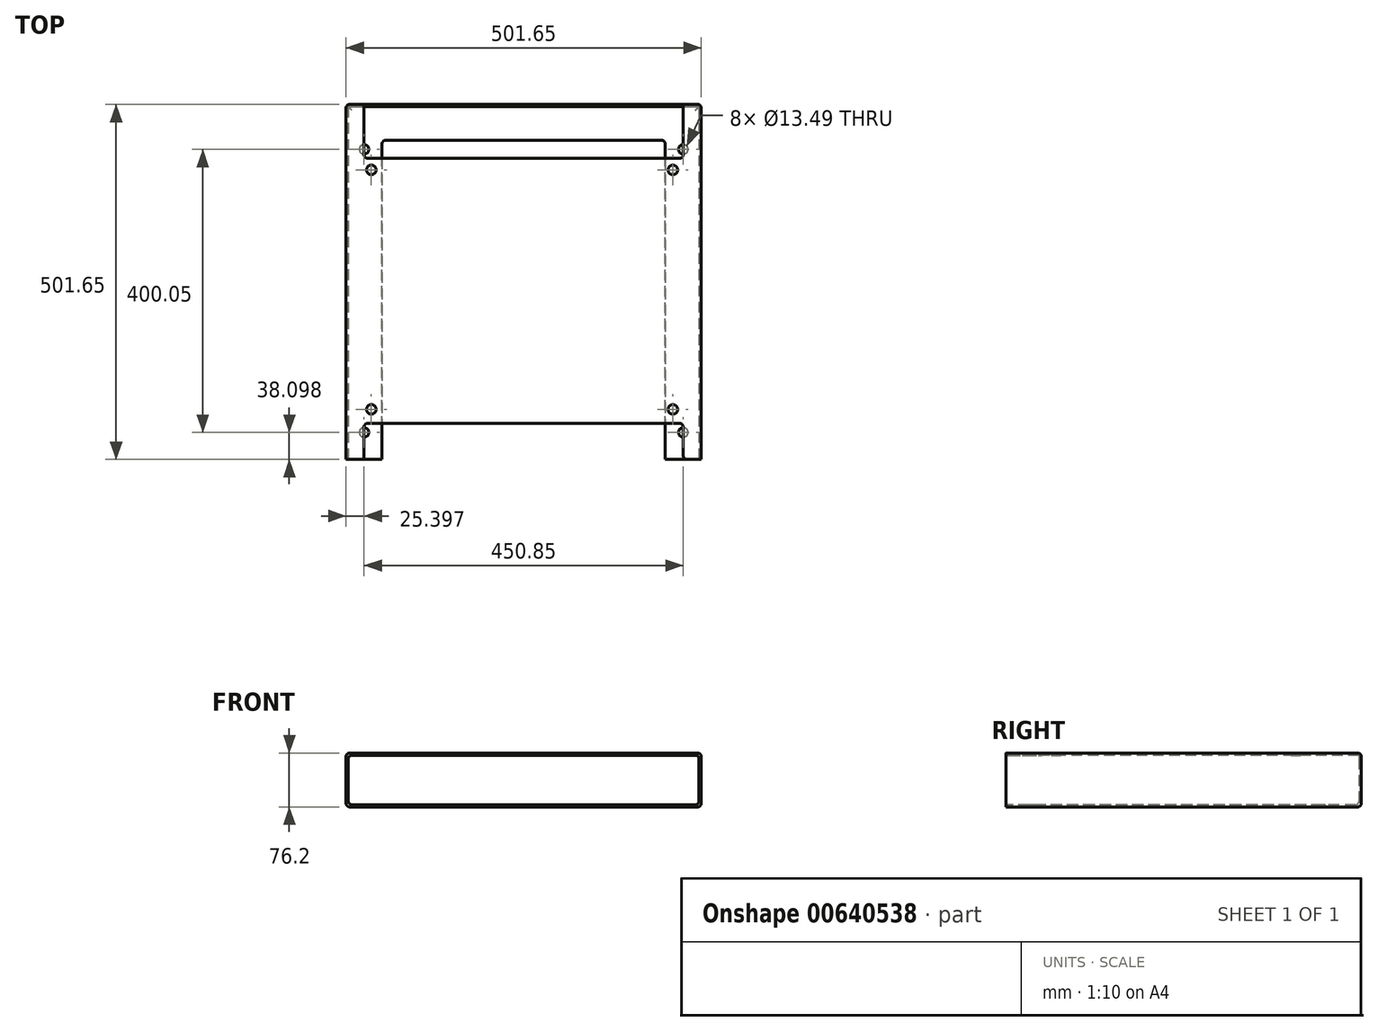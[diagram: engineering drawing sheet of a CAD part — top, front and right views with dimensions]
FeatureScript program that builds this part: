
annotation { "Feature Type Name" : "Feature", "Feature Type Description" : "" }
export const myFeature = defineFeature(function(context is Context, id is Id, definition is map)
    precondition{}
    {
        {
            var Q0;
            Q0=qCreatedBy(makeId("Top.planeOp"),FACE);
            var sketch = newSketch(context, id + "F0", { "sketchPlane" : qUnion([Q0])});
            skLineSegment(sketch, "E0.bottom", {"start": v(-248.23, 375.82) * mm, "end": v(253.42, 375.82) * mm});
            skLineSegment(sketch, "E0.top", {"start": v(-248.23, -125.83) * mm, "end": v(253.42, -125.83) * mm});
            skLineSegment(sketch, "E0.left", {"start": v(-248.23, 375.82) * mm, "end": v(-248.23, -125.83) * mm});
            skLineSegment(sketch, "E0.right", {"start": v(253.42, 375.82) * mm, "end": v(253.42, -125.83) * mm});
            skSolve(sketch);
        }
        {
            var Q0;
            Q0 = qSketchRegion(id + "F0", true);
            extrude(context, id + "F1", {"entities" : qUnion([Q0]), "depth" : 76.2 * mm, "offsetDistance" : 25.4 * mm});
        }
        {
            var Q0;
            Q0=makeQuery(id+"F1.opExtrude","SWEPT_FACE",FACE,{"disambiguationData":[OSD([sQuery(id+"F0.wireOp",EDGE,"E0.top")])]});
            shell(context, id + "F2", {"entities" : qUnion([Q0]), "thickness" : 3.17 * mm});
        }
        {
            var Q0;
            Q0=makeQuery(id+"F1.opExtrude","CAP_FACE",FACE,{"disambiguationData":[OSD([sQuery(id+"F0.wireOp",EDGE,"E0.bottom"),sQuery(id+"F0.wireOp",EDGE,"E0.top"),sQuery(id+"F0.wireOp",EDGE,"E0.left"),sQuery(id+"F0.wireOp",EDGE,"E0.right")])],"isStart":true});
            var sketch = newSketch(context, id + "F3", { "sketchPlane" : qUnion([Q0])});
            skLineSegment(sketch, "E1.bottom", {"start": v(-197.43, 125.83) * mm, "end": v(202.62, 125.83) * mm});
            skLineSegment(sketch, "E1.top", {"start": v(-197.43, -325.02) * mm, "end": v(202.62, -325.02) * mm});
            skLineSegment(sketch, "E1.left", {"start": v(-197.43, 125.83) * mm, "end": v(-197.43, -325.02) * mm});
            skLineSegment(sketch, "E1.right", {"start": v(202.62, 125.83) * mm, "end": v(202.62, -325.02) * mm});
            skSolve(sketch);
        }
        {
            var Q0;
            Q0 = qSketchRegion(id + "F3", true);
            extrude(context, id + "F4", {"entities" : qUnion([Q0]), "operationType" : NewBodyOperationType.REMOVE, "oppositeDirection" : true, "depth" : 25.4 * mm, "offsetDistance" : 25.4 * mm});
        }
        {
            var Q0;
            {var subQ0=sQuery(id+"F0.wireOp",EDGE,"E0.right");var subQ1=sQuery(id+"F0.wireOp",EDGE,"E0.left");var subQ2=sQuery(id+"F0.wireOp",EDGE,"E0.top");var subQ3=sQuery(id+"F0.wireOp",EDGE,"E0.bottom");Q0=makeQuery(id+"F2.opShell","OFFSET_FACE",FACE,{"disambiguationData":[OSD([subQ3,subQ2,subQ1,subQ0]),TDD([makeQuery(id+"F1.opExtrude","CAP_FACE",FACE,{"disambiguationData":[OSD([subQ3,subQ2,subQ1,subQ0])],"isStart":true})])]});}
            var sketch = newSketch(context, id + "F5", { "sketchPlane" : qUnion([Q0])});
            skPoint(sketch, "E2", {"position": v(-222.83, -87.73) * mm});
            skPoint(sketch, "E3", {"position": v(228.02, -87.73) * mm});
            skPoint(sketch, "E4", {"position": v(-222.83, 312.32) * mm});
            skPoint(sketch, "E5", {"position": v(228.02, 312.32) * mm});
            skSolve(sketch);
        }
        {
            var Q0;
            Q0=sQuery(id+"F5.wireOp",VERTEX,"E2");
            var Q1;
            Q1=sQuery(id+"F5.wireOp",VERTEX,"E4");
            var Q2;
            Q2=sQuery(id+"F5.wireOp",VERTEX,"E3");
            var Q3;
            Q3=sQuery(id+"F5.wireOp",VERTEX,"E5");
            var Q4;
            Q4=makeQuery(id+"F1.opExtrude","SWEPT_BODY",BODY,{"disambiguationData":[OSD([sQuery(id+"F0.wireOp",EDGE,"E0.bottom"),sQuery(id+"F0.wireOp",EDGE,"E0.top"),sQuery(id+"F0.wireOp",EDGE,"E0.left"),sQuery(id+"F0.wireOp",EDGE,"E0.right")])]});
            hole(context, id + "F6", {"style" : HoleStyle.SIMPLE, "endStyle" : HoleEndStyle.BLIND, "standardTappedOrClearance" : lookupTablePath({ "standard" : "ANSI", "fit" : "Normal (ASME)", "size" : "1/2", "type" : "Clearance" }), "standardBlindInLast" : lookupTablePath({ "fit" : "Free", "standard" : "ANSI", "size" : "1/2", "type" : "Clearance" }), "holeDiameter" : 13.5 * mm, "majorDiameter" : 6.35 * mm, "holeDepth" : 12.7 * mm, "isTappedThrough" : true, "tappedDepth" : 12.7 * mm, "tapClearance" : 3, "locations" : qUnion([Q0, Q1, Q2, Q3]), "scope" : qUnion([Q4])});
        }
        {
            var Q0;
            Q0=makeQuery(id+"F1.opExtrude","CAP_FACE",FACE,{"disambiguationData":[OSD([sQuery(id+"F0.wireOp",EDGE,"E0.bottom"),sQuery(id+"F0.wireOp",EDGE,"E0.top"),sQuery(id+"F0.wireOp",EDGE,"E0.left"),sQuery(id+"F0.wireOp",EDGE,"E0.right")])],"isStart":false});
            var sketch = newSketch(context, id + "F7", { "sketchPlane" : qUnion([Q0])});
            skLineSegment(sketch, "E6.bottom", {"start": v(-222.83, -125.83) * mm, "end": v(228.02, -125.83) * mm});
            skLineSegment(sketch, "E6.top", {"start": v(-222.83, -75.03) * mm, "end": v(228.02, -75.03) * mm});
            skLineSegment(sketch, "E6.left", {"start": v(-222.83, -125.83) * mm, "end": v(-222.83, -75.03) * mm});
            skLineSegment(sketch, "E6.right", {"start": v(228.02, -125.83) * mm, "end": v(228.02, -75.03) * mm});
            skLineSegment(sketch, "E7.bottom", {"start": v(-222.83, 375.82) * mm, "end": v(228.02, 375.82) * mm});
            skLineSegment(sketch, "E7.top", {"start": v(-222.83, 299.62) * mm, "end": v(228.02, 299.62) * mm});
            skLineSegment(sketch, "E7.left", {"start": v(-222.83, 375.82) * mm, "end": v(-222.83, 299.62) * mm});
            skLineSegment(sketch, "E7.right", {"start": v(228.02, 375.82) * mm, "end": v(228.02, 299.62) * mm});
            skSolve(sketch);
        }
        {
            var Q0;
            Q0 = qSketchRegion(id + "F7", true);
            extrude(context, id + "F8", {"entities" : qUnion([Q0]), "operationType" : NewBodyOperationType.REMOVE, "oppositeDirection" : true, "depth" : 3.17 * mm, "offsetDistance" : 25.4 * mm});
        }
        {
            var Q0;
            Q0=makeQuery(id+"F1.opExtrude","CAP_FACE",FACE,{"disambiguationData":[OSD([sQuery(id+"F0.wireOp",EDGE,"E0.bottom"),sQuery(id+"F0.wireOp",EDGE,"E0.top"),sQuery(id+"F0.wireOp",EDGE,"E0.left"),sQuery(id+"F0.wireOp",EDGE,"E0.right")])],"isStart":false});
            var sketch = newSketch(context, id + "F9", { "sketchPlane" : qUnion([Q0])});
            skPoint(sketch, "E8", {"position": v(213.34, -55.14) * mm});
            skPoint(sketch, "E9", {"position": v(213.34, 283.32) * mm});
            skPoint(sketch, "E10", {"position": v(-212.6, -55.14) * mm});
            skPoint(sketch, "E11", {"position": v(-212.6, 283.32) * mm});
            skSolve(sketch);
        }
        {
            var Q0;
            Q0=sQuery(id+"F9.wireOp",VERTEX,"E8");
            var Q1;
            Q1=sQuery(id+"F9.wireOp",VERTEX,"E9");
            var Q2;
            Q2=sQuery(id+"F9.wireOp",VERTEX,"E11");
            var Q3;
            Q3=sQuery(id+"F9.wireOp",VERTEX,"E10");
            var Q4;
            Q4=makeQuery(id+"F1.opExtrude","SWEPT_BODY",BODY,{"disambiguationData":[OSD([sQuery(id+"F0.wireOp",EDGE,"E0.bottom"),sQuery(id+"F0.wireOp",EDGE,"E0.top"),sQuery(id+"F0.wireOp",EDGE,"E0.left"),sQuery(id+"F0.wireOp",EDGE,"E0.right")])]});
            hole(context, id + "F10", {"style" : HoleStyle.SIMPLE, "endStyle" : HoleEndStyle.BLIND, "standardTappedOrClearance" : lookupTablePath({ "standard" : "ANSI", "fit" : "Normal (ASME)", "size" : "1/2", "type" : "Clearance" }), "standardBlindInLast" : lookupTablePath({ "fit" : "Free", "standard" : "ANSI", "size" : "1/2", "type" : "Clearance" }), "holeDiameter" : 13.5 * mm, "majorDiameter" : 6.35 * mm, "holeDepth" : 12.7 * mm, "isTappedThrough" : true, "tappedDepth" : 12.7 * mm, "tapClearance" : 3, "locations" : qUnion([Q0, Q1, Q2, Q3]), "scope" : qUnion([Q4])});
        }
        {
            var Q0;
            {var subQ0=sQuery(id+"F0.wireOp",EDGE,"E0.left");Q0=makeQuery(id+"F2.opShell","OFFSET_EDGE",EDGE,{"disambiguationData":[OSD([subQ0]),TDD([makeQuery(id+"F1.opExtrude","CAP_EDGE",EDGE,{"disambiguationData":[OSD([subQ0])],"isStart":true})])]});}
            var Q1;
            {var subQ0=sQuery(id+"F0.wireOp",EDGE,"E0.right");Q1=makeQuery(id+"F2.opShell","OFFSET_EDGE",EDGE,{"disambiguationData":[OSD([subQ0]),TDD([makeQuery(id+"F1.opExtrude","CAP_EDGE",EDGE,{"disambiguationData":[OSD([subQ0])],"isStart":true})])]});}
            var Q2;
            {var subQ0=sQuery(id+"F0.wireOp",EDGE,"E0.bottom");Q2=makeQuery(id+"F2.opShell","OFFSET_EDGE",EDGE,{"disambiguationData":[OSD([subQ0]),TDD([makeQuery(id+"F1.opExtrude","CAP_EDGE",EDGE,{"disambiguationData":[OSD([subQ0])],"isStart":true})])]});}
            var Q3;
            {var subQ0=sQuery(id+"F0.wireOp",EDGE,"E0.left");Q3=makeQuery(id+"F2.opShell","OFFSET_EDGE",EDGE,{"disambiguationData":[OSD([subQ0]),TDD([makeQuery(id+"F1.opExtrude","CAP_EDGE",EDGE,{"disambiguationData":[OSD([subQ0])],"isStart":false})])]});}
            var Q4;
            {var subQ0=sQuery(id+"F0.wireOp",EDGE,"E0.right");Q4=makeQuery(id+"F2.opShell","OFFSET_EDGE",EDGE,{"disambiguationData":[OSD([subQ0]),TDD([makeQuery(id+"F1.opExtrude","CAP_EDGE",EDGE,{"disambiguationData":[OSD([subQ0])],"isStart":false})])]});}
            var Q5;
            Q5=makeQuery(id+"F1.opExtrude","SWEPT_EDGE",EDGE,{"disambiguationData":[OSD([sQuery(id+"F0.wireOp",EDGE,"E0.bottom"),sQuery(id+"F0.wireOp",EDGE,"E0.left")])]});
            var Q6;
            Q6=makeQuery(id+"F1.opExtrude","SWEPT_EDGE",EDGE,{"disambiguationData":[OSD([sQuery(id+"F0.wireOp",EDGE,"E0.bottom"),sQuery(id+"F0.wireOp",EDGE,"E0.right")])]});
            var Q7;
            Q7=makeQuery(id+"F1.opExtrude","CAP_EDGE",EDGE,{"disambiguationData":[OSD([sQuery(id+"F0.wireOp",EDGE,"E0.left")])],"isStart":false});
            var Q8;
            Q8=makeQuery(id+"F1.opExtrude","CAP_EDGE",EDGE,{"disambiguationData":[OSD([sQuery(id+"F0.wireOp",EDGE,"E0.left")])],"isStart":true});
            var Q9;
            Q9=makeQuery(id+"F1.opExtrude","CAP_EDGE",EDGE,{"disambiguationData":[OSD([sQuery(id+"F0.wireOp",EDGE,"E0.right")])],"isStart":true});
            var Q10;
            Q10=makeQuery(id+"F1.opExtrude","CAP_EDGE",EDGE,{"disambiguationData":[OSD([sQuery(id+"F0.wireOp",EDGE,"E0.right")])],"isStart":false});
            var Q11;
            {var subQ0=sQuery(id+"F0.wireOp",EDGE,"E0.bottom");var subQ1=sQuery(id+"F0.wireOp",EDGE,"E0.right");Q11=makeQuery(id+"F8.boolean.opBoolean","SPLIT",EDGE,{"disambiguationData":[TD([makeQuery(id+"F1.opExtrude","SWEPT_FACE",FACE,{"disambiguationData":[OSD([subQ1])]})])],"derivedFrom":makeQuery(id+"F1.opExtrude","CAP_EDGE",EDGE,{"disambiguationData":[OSD([subQ0])],"isStart":false})});}
            var Q12;
            {var subQ0=sQuery(id+"F0.wireOp",EDGE,"E0.bottom");var subQ1=sQuery(id+"F0.wireOp",EDGE,"E0.left");Q12=makeQuery(id+"F8.boolean.opBoolean","SPLIT",EDGE,{"disambiguationData":[TD([makeQuery(id+"F1.opExtrude","SWEPT_FACE",FACE,{"disambiguationData":[OSD([subQ1])]})])],"derivedFrom":makeQuery(id+"F1.opExtrude","CAP_EDGE",EDGE,{"disambiguationData":[OSD([subQ0])],"isStart":false})});}
            var Q13;
            Q13=makeQuery(id+"F8.boolean.opBoolean","COPY",EDGE,{"derivedFrom":makeQuery(id+"F8.opExtrude","SWEPT_EDGE",EDGE,{"disambiguationData":[OSD([sQuery(id+"F0.wireOp",EDGE,"E0.top"),sQuery(id+"F7.wireOp",EDGE,"E6.bottom"),sQuery(id+"F7.wireOp",EDGE,"E6.left")])]})});
            var Q14;
            Q14=makeQuery(id+"F8.boolean.opBoolean","COPY",EDGE,{"derivedFrom":makeQuery(id+"F8.opExtrude","SWEPT_EDGE",EDGE,{"disambiguationData":[OSD([sQuery(id+"F7.wireOp",EDGE,"E6.top"),sQuery(id+"F7.wireOp",EDGE,"E6.left")])]})});
            var Q15;
            Q15=makeQuery(id+"F4.boolean.opBoolean","COPY",EDGE,{"derivedFrom":makeQuery(id+"F4.opExtrude","SWEPT_EDGE",EDGE,{"disambiguationData":[OSD([sQuery(id+"F0.wireOp",EDGE,"E0.top"),sQuery(id+"F3.wireOp",EDGE,"E1.bottom"),sQuery(id+"F3.wireOp",EDGE,"E1.left")])]})});
            var Q16;
            Q16=makeQuery(id+"F4.boolean.opBoolean","COPY",EDGE,{"derivedFrom":makeQuery(id+"F4.opExtrude","SWEPT_EDGE",EDGE,{"disambiguationData":[OSD([sQuery(id+"F0.wireOp",EDGE,"E0.top"),sQuery(id+"F3.wireOp",EDGE,"E1.bottom"),sQuery(id+"F3.wireOp",EDGE,"E1.right")])]})});
            var Q17;
            Q17=makeQuery(id+"F8.boolean.opBoolean","COPY",EDGE,{"derivedFrom":makeQuery(id+"F8.opExtrude","SWEPT_EDGE",EDGE,{"disambiguationData":[OSD([sQuery(id+"F0.wireOp",EDGE,"E0.top"),sQuery(id+"F7.wireOp",EDGE,"E6.bottom"),sQuery(id+"F7.wireOp",EDGE,"E6.right")])]})});
            var Q18;
            Q18=makeQuery(id+"F8.boolean.opBoolean","COPY",EDGE,{"derivedFrom":makeQuery(id+"F8.opExtrude","SWEPT_EDGE",EDGE,{"disambiguationData":[OSD([sQuery(id+"F7.wireOp",EDGE,"E6.top"),sQuery(id+"F7.wireOp",EDGE,"E6.right")])]})});
            var Q19;
            Q19=makeQuery(id+"F8.boolean.opBoolean","COPY",EDGE,{"derivedFrom":makeQuery(id+"F8.opExtrude","SWEPT_EDGE",EDGE,{"disambiguationData":[OSD([sQuery(id+"F7.wireOp",EDGE,"E7.top"),sQuery(id+"F7.wireOp",EDGE,"E7.right")])]})});
            var Q20;
            Q20=makeQuery(id+"F8.boolean.opBoolean","COPY",EDGE,{"derivedFrom":makeQuery(id+"F8.opExtrude","SWEPT_EDGE",EDGE,{"disambiguationData":[OSD([sQuery(id+"F7.wireOp",EDGE,"E7.top"),sQuery(id+"F7.wireOp",EDGE,"E7.left")])]})});
            var Q21;
            Q21=makeQuery(id+"F4.boolean.opBoolean","COPY",EDGE,{"derivedFrom":makeQuery(id+"F4.opExtrude","SWEPT_EDGE",EDGE,{"disambiguationData":[OSD([sQuery(id+"F3.wireOp",EDGE,"E1.top"),sQuery(id+"F3.wireOp",EDGE,"E1.left")])]})});
            var Q22;
            Q22=makeQuery(id+"F4.boolean.opBoolean","COPY",EDGE,{"derivedFrom":makeQuery(id+"F4.opExtrude","SWEPT_EDGE",EDGE,{"disambiguationData":[OSD([sQuery(id+"F3.wireOp",EDGE,"E1.top"),sQuery(id+"F3.wireOp",EDGE,"E1.right")])]})});
            var Q23;
            Q23=makeQuery(id+"F1.opExtrude","CAP_EDGE",EDGE,{"disambiguationData":[OSD([sQuery(id+"F0.wireOp",EDGE,"E0.bottom")])],"isStart":true});
            fillet(context, id + "F11", {"entities" : qUnion([Q0, Q1, Q2, Q3, Q4, Q5, Q6, Q7, Q8, Q9, Q10, Q11, Q12, Q13, Q14, Q15, Q16, Q17, Q18, Q19, Q20, Q21, Q22, Q23]), "radius" : 5.08 * mm, "tangentPropagation" : true, "allowEdgeOverflow" : false});
        }
    });
